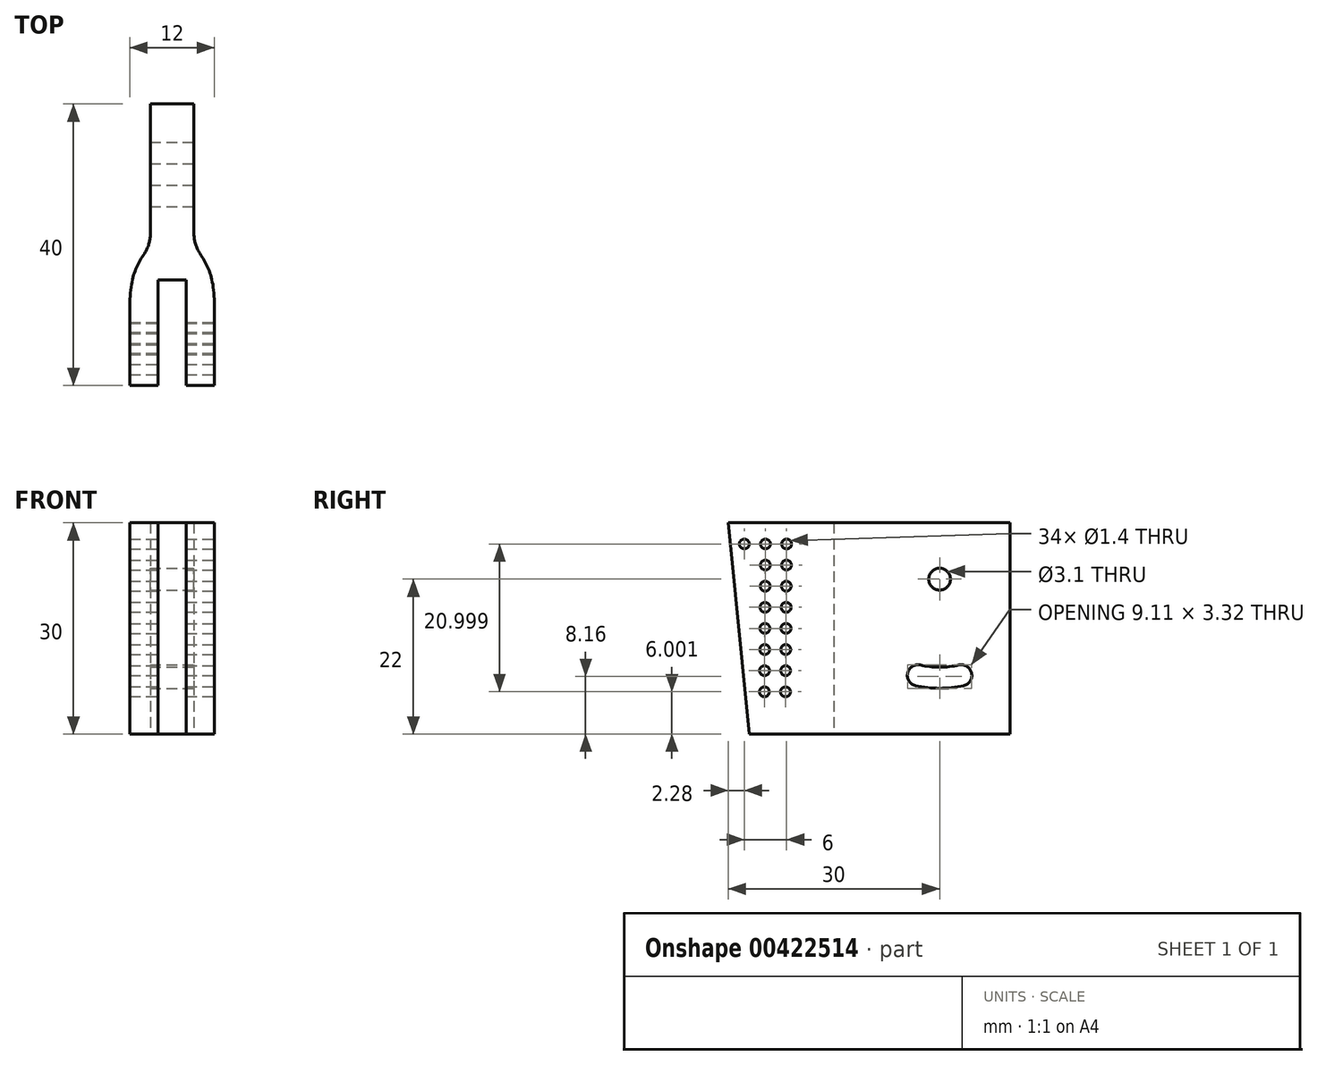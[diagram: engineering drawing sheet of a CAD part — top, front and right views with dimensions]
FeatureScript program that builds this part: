
annotation { "Feature Type Name" : "Feature", "Feature Type Description" : "" }
export const myFeature = defineFeature(function(context is Context, id is Id, definition is map)
    precondition{}
    {
        {
            var Q0;
            Q0=qCreatedBy(makeId("Top.planeOp"),FACE);
            var sketch = newSketch(context, id + "F0", { "sketchPlane" : qUnion([Q0])});
            skLineSegment(sketch, "E0", {"start": v(0, 0) * mm, "end": v(0, 41.14) * mm, "construction": true});
            skLineSegment(sketch, "E1", {"start": v(0, 40) * mm, "end": v(3.1, 40) * mm});
            skLineSegment(sketch, "E2", {"start": v(3.1, 40) * mm, "end": v(3.1, 21.54) * mm});
            skLineSegment(sketch, "E3", {"start": v(6, 11.28) * mm, "end": v(6, 0) * mm});
            skLineSegment(sketch, "E4", {"start": v(0, 15) * mm, "end": v(2, 15) * mm});
            skLineSegment(sketch, "E5", {"start": v(2, 15) * mm, "end": v(2, 0) * mm});
            skLineSegment(sketch, "E6", {"start": v(2, 0) * mm, "end": v(6, 0) * mm});
            skFitSpline(sketch, "E7", {"points": [v(3.1, 20) * mm, v(6, 11.28) * mm], "startDerivative": vector(4.98, -7.34) * mm, "endDerivative": vector(0.02, -14.52) * mm});
            skArc(sketch, "E8.filletArc", {"start": v(3.1, 21.54) * mm, "mid": v(3.31, 20.1) * mm, "end": v(3.94, 18.77) * mm});
            skLineSegment(sketch, "E9.MirrorCS", {"start": v(0, 40) * mm, "end": v(-3.1, 40) * mm});
            skLineSegment(sketch, "E10.MirrorCS", {"start": v(-3.1, 40) * mm, "end": v(-3.1, 21.54) * mm});
            skArc(sketch, "E11.MirrorCS", {"start": v(-3.1, 21.54) * mm, "mid": v(-3.31, 20.1) * mm, "end": v(-3.94, 18.77) * mm});
            skFitSpline(sketch, "E12.MirrorCS", {"points": [v(-3.1, 20) * mm, v(-6, 11.28) * mm], "startDerivative": vector(-4.98, -7.34) * mm, "endDerivative": vector(-0.02, -14.52) * mm});
            skLineSegment(sketch, "E13.MirrorCS", {"start": v(-6, 11.28) * mm, "end": v(-6, 0) * mm});
            skLineSegment(sketch, "E14.MirrorCS", {"start": v(-2, 0) * mm, "end": v(-6, 0) * mm});
            skLineSegment(sketch, "E15.MirrorCS", {"start": v(-2, 15) * mm, "end": v(-2, 0) * mm});
            skLineSegment(sketch, "E16.MirrorCS", {"start": v(0, 15) * mm, "end": v(-2, 15) * mm});
            skSolve(sketch);
        }
        {
            var Q0;
            Q0 = qSketchRegion(id + "F0", true);
            extrude(context, id + "F1", {"entities" : qUnion([Q0]), "depth" : 30 * mm});
        }
        {
            var Q0;
            Q0=makeQuery(id+"F1.opExtrude","SWEPT_FACE",FACE,{"disambiguationData":[OSD([sQuery(id+"F0.wireOp",EDGE,"E2")])]});
            var sketch = newSketch(context, id + "F2", { "sketchPlane" : qUnion([Q0])});
            skLineSegment(sketch, "E17.0", {"start": v(30, 25) * mm, "end": v(30, 0) * mm, "construction": true});
            skLineSegment(sketch, "E18.0", {"start": v(40, 22) * mm, "end": v(21.54, 22) * mm, "construction": true});
            skLineSegment(sketch, "E19.0", {"start": v(40, 8) * mm, "end": v(21.54, 8) * mm, "construction": true});
            skCircle(sketch, "E20", {"center": v(30, 22) * mm, "radius": 1.55 * mm});
            skLineSegment(sketch, "E21", {"start": v(30, 22) * mm, "end": v(33.66, 5.77) * mm, "construction": true});
            skArc(sketch, "E22", {"start": v(33.4, 6.88) * mm, "mid": v(34.54, 8.67) * mm, "end": v(32.75, 9.8) * mm});
            skArc(sketch, "E23.MirrorC", {"start": v(26.6, 6.88) * mm, "mid": v(25.46, 8.67) * mm, "end": v(27.25, 9.8) * mm});
            skArc(sketch, "E24", {"start": v(27.25, 9.8) * mm, "mid": v(30, 9.5) * mm, "end": v(32.75, 9.8) * mm});
            skArc(sketch, "E25", {"start": v(26.6, 6.88) * mm, "mid": v(30, 6.5) * mm, "end": v(33.4, 6.88) * mm});
            skSolve(sketch);
        }
        {
            var Q0;
            Q0 = qSketchRegion(id + "F2", true);
            extrude(context, id + "F3", {"entities" : qUnion([Q0]), "operationType" : NewBodyOperationType.REMOVE, "oppositeDirection" : true, "depth" : 25 * mm});
        }
        {
            var Q0;
            Q0=makeQuery(id+"F1.opExtrude","SWEPT_FACE",FACE,{"disambiguationData":[OSD([sQuery(id+"F0.wireOp",EDGE,"E3")])]});
            var sketch = newSketch(context, id + "F4", { "sketchPlane" : qUnion([Q0])});
            skLineSegment(sketch, "E26.0", {"start": v(0, 30) * mm, "end": v(0, 0) * mm});
            skLineSegment(sketch, "E27.0", {"start": v(3, 30) * mm, "end": v(3, 0) * mm, "construction": true});
            skLineSegment(sketch, "E28", {"start": v(0, 30) * mm, "end": v(3, 0) * mm});
            skLineSegment(sketch, "E29", {"start": v(3, 0) * mm, "end": v(0, 0) * mm});
            skSolve(sketch);
        }
        {
            var Q0;
            Q0 = qSketchRegion(id + "F4", true);
            extrude(context, id + "F5", {"entities" : qUnion([Q0]), "operationType" : NewBodyOperationType.REMOVE, "oppositeDirection" : true, "depth" : 25 * mm});
        }
        {
            var Q0;
            Q0=makeQuery(id+"F1.opExtrude","SWEPT_FACE",FACE,{"disambiguationData":[OSD([sQuery(id+"F0.wireOp",EDGE,"E3")])]});
            var sketch = newSketch(context, id + "F6", { "sketchPlane" : qUnion([Q0])});
            skLineSegment(sketch, "E30.0", {"start": v(11.28, 30) * mm, "end": v(0, 30) * mm, "construction": true});
            skLineSegment(sketch, "E31.0", {"start": v(11.28, 30) * mm, "end": v(11.28, 0) * mm, "construction": true});
            skLineSegment(sketch, "E32.0", {"start": v(11.28, 27) * mm, "end": v(0, 27) * mm, "construction": true});
            skLineSegment(sketch, "E33.0", {"start": v(8.28, 30) * mm, "end": v(8.28, 0) * mm, "construction": true});
            skCircle(sketch, "E34", {"center": v(8.28, 27) * mm, "radius": 0.7 * mm});
            skCircle(sketch, "E35.1.0.0", {"center": v(5.28, 27) * mm, "radius": 0.7 * mm});
            skCircle(sketch, "E35.2.0.0", {"center": v(2.28, 27) * mm, "radius": 0.7 * mm});
            skLineSegment(sketch, "E35.direction1", {"start": v(8.28, 27) * mm, "end": v(5.28, 27) * mm, "construction": true});
            skCircle(sketch, "E36.1.0.0", {"center": v(5.26, 24) * mm, "radius": 0.7 * mm});
            skCircle(sketch, "E36.1.0.1", {"center": v(8.26, 24) * mm, "radius": 0.7 * mm});
            skCircle(sketch, "E36.2.0.0", {"center": v(5.23, 21) * mm, "radius": 0.7 * mm});
            skCircle(sketch, "E36.2.0.1", {"center": v(8.23, 21) * mm, "radius": 0.7 * mm});
            skCircle(sketch, "E36.3.0.0", {"center": v(5.21, 18) * mm, "radius": 0.7 * mm});
            skCircle(sketch, "E36.3.0.1", {"center": v(8.21, 18) * mm, "radius": 0.7 * mm});
            skCircle(sketch, "E36.4.0.0", {"center": v(5.19, 15) * mm, "radius": 0.7 * mm});
            skCircle(sketch, "E36.4.0.1", {"center": v(8.19, 15) * mm, "radius": 0.7 * mm});
            skCircle(sketch, "E36.5.0.0", {"center": v(5.17, 12) * mm, "radius": 0.7 * mm});
            skCircle(sketch, "E36.5.0.1", {"center": v(8.17, 12) * mm, "radius": 0.7 * mm});
            skCircle(sketch, "E36.6.0.0", {"center": v(5.14, 9) * mm, "radius": 0.7 * mm});
            skCircle(sketch, "E36.6.0.1", {"center": v(8.14, 9) * mm, "radius": 0.7 * mm});
            skCircle(sketch, "E36.7.0.0", {"center": v(5.12, 6) * mm, "radius": 0.7 * mm});
            skCircle(sketch, "E36.7.0.1", {"center": v(8.12, 6) * mm, "radius": 0.7 * mm});
            skLineSegment(sketch, "E36.direction1", {"start": v(5.28, 27) * mm, "end": v(5.26, 24) * mm, "construction": true});
            skSolve(sketch);
        }
        {
            var Q0;
            Q0 = qSketchRegion(id + "F6", true);
            extrude(context, id + "F7", {"entities" : qUnion([Q0]), "operationType" : NewBodyOperationType.REMOVE, "oppositeDirection" : true, "depth" : 25 * mm});
        }
    });
